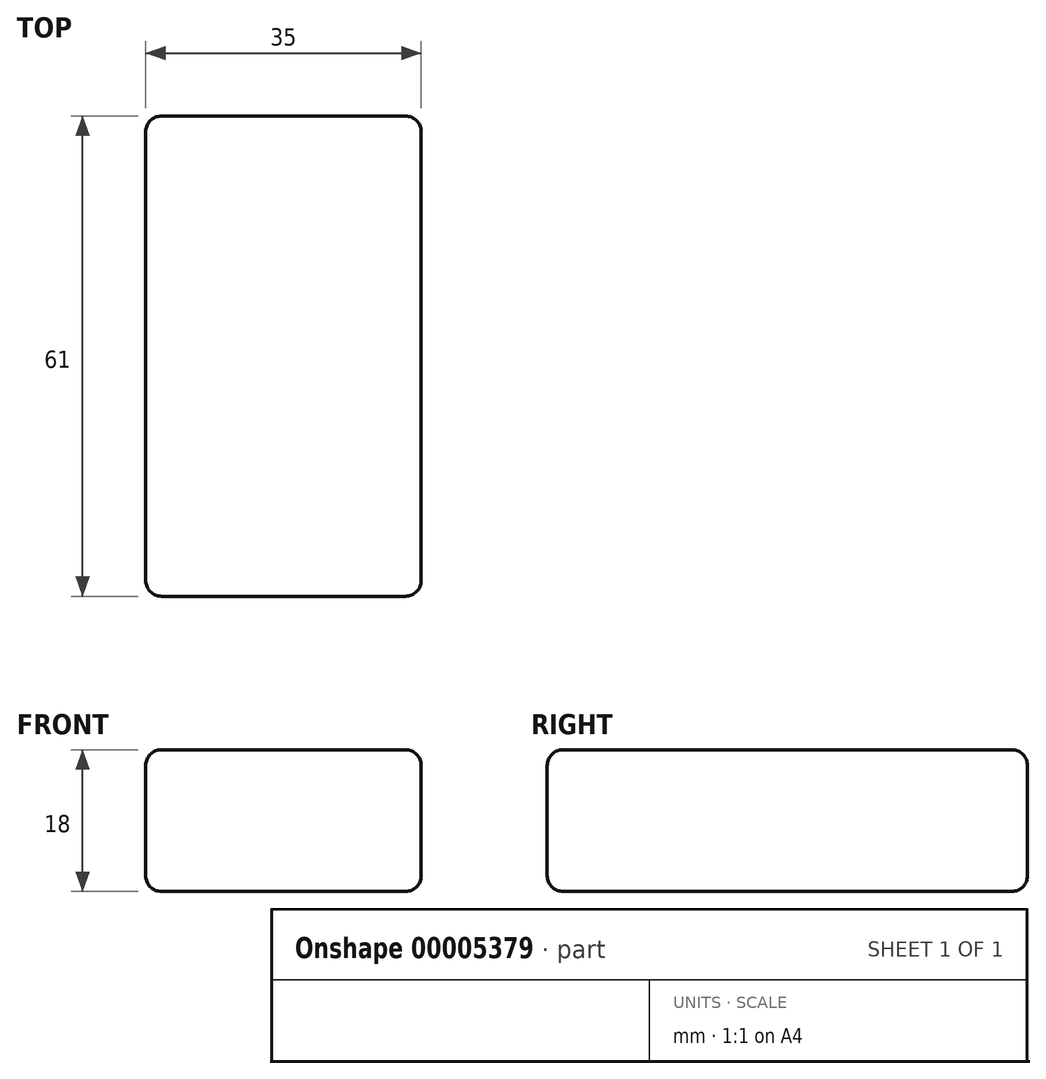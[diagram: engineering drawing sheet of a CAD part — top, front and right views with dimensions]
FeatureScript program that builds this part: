
annotation { "Feature Type Name" : "Feature", "Feature Type Description" : "" }
export const myFeature = defineFeature(function(context is Context, id is Id, definition is map)
    precondition{}
    {
        {
            var Q0;
            Q0=qCreatedBy(makeId("Top.planeOp"),FACE);
            var sketch = newSketch(context, id + "F0", { "sketchPlane" : qUnion([Q0])});
            skLineSegment(sketch, "E0.bottom", {"start": v(-17.83, 28.62) * mm, "end": v(17.17, 28.62) * mm});
            skLineSegment(sketch, "E0.top", {"start": v(-17.83, -32.38) * mm, "end": v(17.17, -32.38) * mm});
            skLineSegment(sketch, "E0.left", {"start": v(-17.83, 28.62) * mm, "end": v(-17.83, -32.38) * mm});
            skLineSegment(sketch, "E0.right", {"start": v(17.17, 28.62) * mm, "end": v(17.17, -32.38) * mm});
            skSolve(sketch);
        }
        {
            var Q0;
            Q0 = qSketchRegion(id + "F0", true);
            extrude(context, id + "F1", {"entities" : qUnion([Q0]), "depth" : 18 * mm});
        }
        {
            var Q0;
            Q0=makeQuery(id+"F1.opExtrude","SWEPT_EDGE",EDGE,{"disambiguationData":[OSD([sQuery(id+"F0.wireOp",EDGE,"E0.top"),sQuery(id+"F0.wireOp",EDGE,"E0.left")])]});
            var Q1;
            Q1=makeQuery(id+"F1.opExtrude","SWEPT_EDGE",EDGE,{"disambiguationData":[OSD([sQuery(id+"F0.wireOp",EDGE,"E0.top"),sQuery(id+"F0.wireOp",EDGE,"E0.right")])]});
            var Q2;
            Q2=makeQuery(id+"F1.opExtrude","SWEPT_EDGE",EDGE,{"disambiguationData":[OSD([sQuery(id+"F0.wireOp",EDGE,"E0.bottom"),sQuery(id+"F0.wireOp",EDGE,"E0.right")])]});
            var Q3;
            Q3=makeQuery(id+"F1.opExtrude","SWEPT_EDGE",EDGE,{"disambiguationData":[OSD([sQuery(id+"F0.wireOp",EDGE,"E0.bottom"),sQuery(id+"F0.wireOp",EDGE,"E0.left")])]});
            var Q4;
            Q4=makeQuery(id+"F1.opExtrude","CAP_EDGE",EDGE,{"disambiguationData":[OSD([sQuery(id+"F0.wireOp",EDGE,"E0.right")])],"isStart":false});
            var Q5;
            Q5=makeQuery(id+"F1.opExtrude","CAP_EDGE",EDGE,{"disambiguationData":[OSD([sQuery(id+"F0.wireOp",EDGE,"E0.bottom")])],"isStart":false});
            var Q6;
            Q6=makeQuery(id+"F1.opExtrude","CAP_EDGE",EDGE,{"disambiguationData":[OSD([sQuery(id+"F0.wireOp",EDGE,"E0.top")])],"isStart":false});
            var Q7;
            Q7=makeQuery(id+"F1.opExtrude","CAP_EDGE",EDGE,{"disambiguationData":[OSD([sQuery(id+"F0.wireOp",EDGE,"E0.left")])],"isStart":false});
            var Q8;
            Q8=makeQuery(id+"F1.opExtrude","CAP_EDGE",EDGE,{"disambiguationData":[OSD([sQuery(id+"F0.wireOp",EDGE,"E0.top")])],"isStart":true});
            var Q9;
            Q9=makeQuery(id+"F1.opExtrude","CAP_EDGE",EDGE,{"disambiguationData":[OSD([sQuery(id+"F0.wireOp",EDGE,"E0.left")])],"isStart":true});
            var Q10;
            Q10=makeQuery(id+"F1.opExtrude","CAP_EDGE",EDGE,{"disambiguationData":[OSD([sQuery(id+"F0.wireOp",EDGE,"E0.bottom")])],"isStart":true});
            var Q11;
            Q11=makeQuery(id+"F1.opExtrude","CAP_EDGE",EDGE,{"disambiguationData":[OSD([sQuery(id+"F0.wireOp",EDGE,"E0.right")])],"isStart":true});
            fillet(context, id + "F2", {"entities" : qUnion([Q0, Q1, Q2, Q3, Q4, Q5, Q6, Q7, Q8, Q9, Q10, Q11]), "radius" : 2 * mm, "tangentPropagation" : true, "allowEdgeOverflow" : false});
        }
    });
